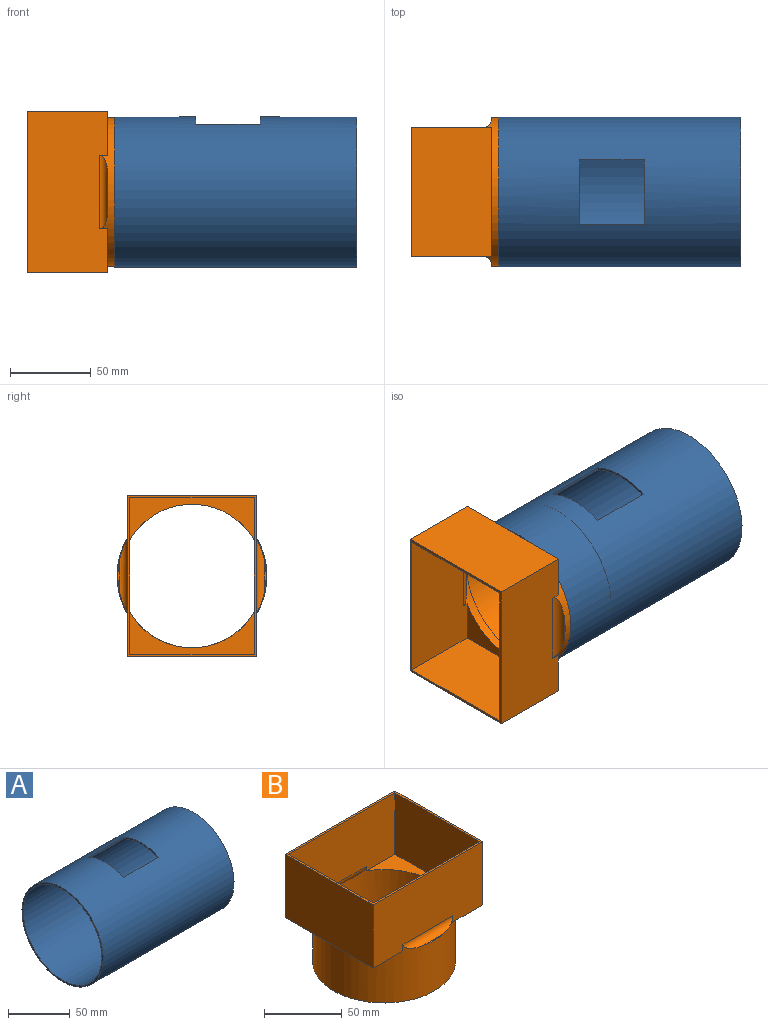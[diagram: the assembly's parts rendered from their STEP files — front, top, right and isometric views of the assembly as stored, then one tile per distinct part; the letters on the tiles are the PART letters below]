
ASSEMBLY  parts=2 mates=1
PART A: 8 faces, bbox 150x93x93 mm
  f0: plane 93x93mm, normal (-1,0,0), area 431.2mm2, adj f2,f3
  f1: plane 93x93mm, normal (1,0,0), area 431.2mm2, adj f2,f3
  f2: cylinder r=46.5mm len=150mm, axis (1,0,0), area 42171.3mm2, adj f0,f1,f4,f5,f6,f7
  f3: cylinder r=45mm len=150mm, axis (1,0,0), area 40753.5mm2, adj f0,f1,f4,f5,f6,f7
  f4: plane 40x1.67mm, normal (0,1,0), area 66.7mm2, adj f2,f3,f5,f7
  f5: plane 40x6.19mm, normal (-1,0,0), area 62.1mm2, adj f2,f3,f4,f6
  f6: plane 40x1.67mm, normal (0,-1,0), area 66.7mm2, adj f2,f3,f5,f7
  f7: plane 40x6.19mm, normal (1,0,0), area 62.1mm2, adj f2,f3,f4,f6
PART B: 22 faces, bbox 100x92x90 mm
  f0: plane 100x80mm, normal (0,0,1), area 531mm2, adj f2,f3,f4,f5,f14,f15,f16,f17
  f1: plane 80x27.28mm, normal (0,0,-1), area 860.4mm2, adj f2,f4,f5,f8
  f2: plane 100x50mm, normal (0,-1,0), area 4772.8mm2, adj f0,f1,f3,f5,f6,f8,f12
  f3: plane 80x50mm, normal (1,0,0), area 4000mm2, adj f0,f2,f4,f6
  f4: plane 100x50mm, normal (0,1,0), area 4772.8mm2, adj f0,f1,f3,f5,f6,f8,f11
  f5: plane 80x50mm, normal (-1,0,0), area 4000mm2, adj f0,f1,f2,f4
  f6: plane 80x27.28mm, normal (0,0,-1), area 860.4mm2, adj f2,f3,f4,f8
  f7: plane 19.08x1mm, normal (0,0,1), area 12.7mm2, adj f8,f11
  f8: cylinder r=46mm len=92mm, axis (0,0,1), area 11609.8mm2, adj f1,f2,f4,f6,f7,f9,f10,f11
  f9: plane 92x92mm, normal (0,0,-1), area 426.5mm2, adj f8,f19
  f10: plane 19.08x1mm, normal (0,0,1), area 12.7mm2, adj f8,f12
  f11: cylinder r=5mm len=45.43mm, axis (-1,0,0), area 294.3mm2, adj f4,f7,f8
  f12: cylinder r=5mm len=45.43mm, axis (1,0,0), area 294.3mm2, adj f2,f8,f10
  f13: plane 77x26.18mm, normal (0,0,1), area 805mm2, adj f14,f16,f17,f19
  f14: plane 97x48.5mm, normal (0,1,0), area 4548.3mm2, adj f0,f13,f15,f17,f18,f19,f21
  f15: plane 77x48.5mm, normal (-1,0,0), area 3734.5mm2, adj f0,f14,f16,f18
  f16: plane 97x48.5mm, normal (0,-1,0), area 4548.3mm2, adj f0,f13,f15,f17,f18,f19,f20
  f17: plane 77x48.5mm, normal (1,0,0), area 3734.5mm2, adj f0,f13,f14,f16
  f18: plane 77x26.18mm, normal (0,0,1), area 805mm2, adj f14,f15,f16,f19
  f19: cylinder r=44.5mm len=89mm, axis (0,0,1), area 11409.4mm2, adj f9,f13,f14,f16,f18,f20,f21
  f20: cylinder r=6.5mm len=44.63mm, axis (-1,0,0), area 334.8mm2, adj f16,f19
  f21: cylinder r=6.5mm len=44.63mm, axis (1,0,0), area 334.8mm2, adj f14,f19
PLACE A t=(-5.14,11.31,-16.74)mm
PLACE B rot(axis=(0.71,0,-0.71),180deg) t=(-9.66,11.31,-16.74)mm
MATE cylindrical B.f8 <-> A.f2  axis (-1,0,0) through (7.71,11.31,-16.74)mm
